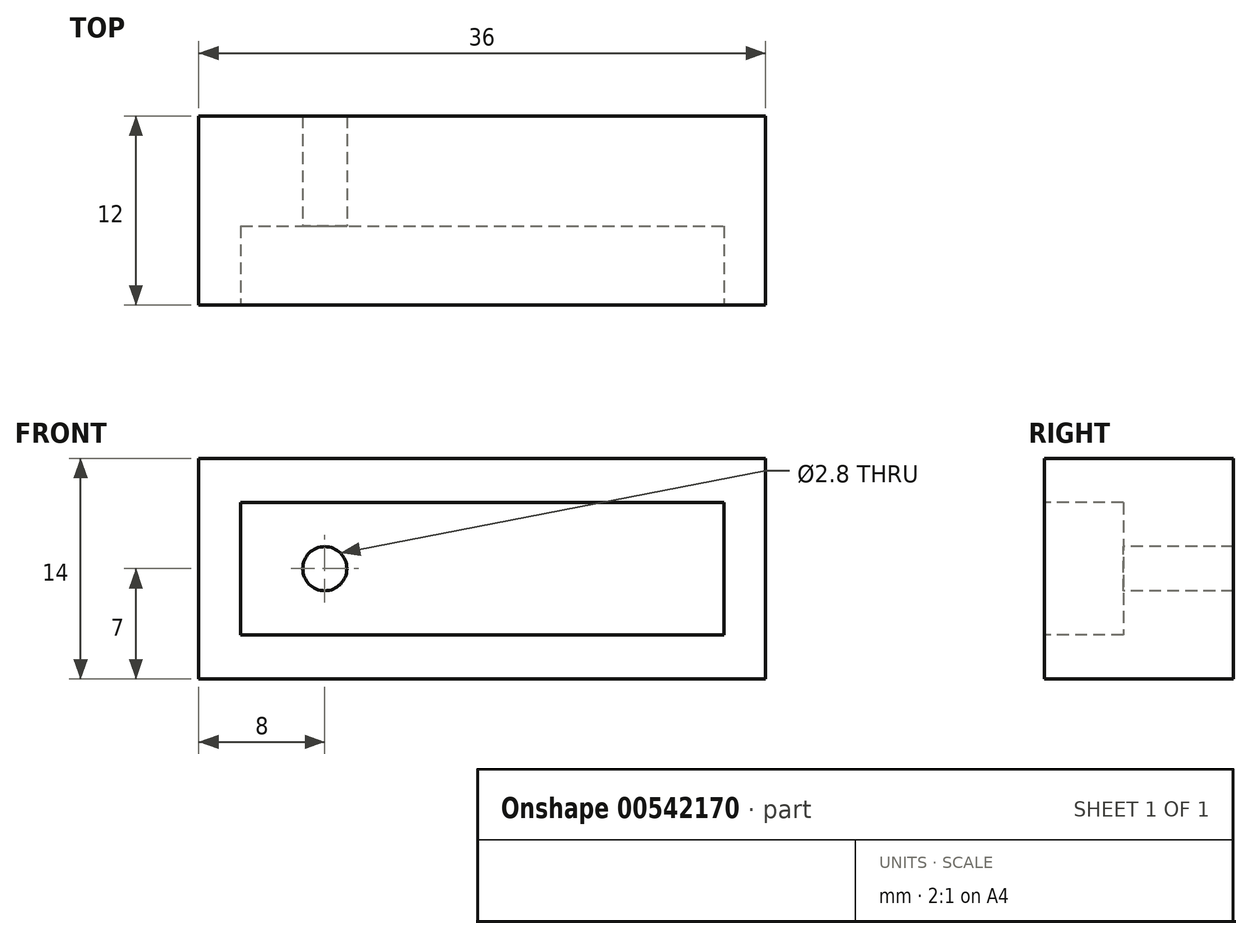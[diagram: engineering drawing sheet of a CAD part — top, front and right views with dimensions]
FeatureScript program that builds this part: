
annotation { "Feature Type Name" : "Feature", "Feature Type Description" : "" }
export const myFeature = defineFeature(function(context is Context, id is Id, definition is map)
    precondition{}
    {
        {
            var Q0;
            Q0=qCreatedBy(makeId("Front.planeOp"),FACE);
            var sketch = newSketch(context, id + "F0", { "sketchPlane" : qUnion([Q0])});
            skLineSegment(sketch, "E0.bottom", {"start": v(-18, 7) * mm, "end": v(18, 7) * mm});
            skLineSegment(sketch, "E0.top", {"start": v(-18, -7) * mm, "end": v(18, -7) * mm});
            skLineSegment(sketch, "E0.left", {"start": v(-18, 7) * mm, "end": v(-18, -7) * mm});
            skLineSegment(sketch, "E0.right", {"start": v(18, 7) * mm, "end": v(18, -7) * mm});
            skSolve(sketch);
        }
        {
            var Q0;
            Q0 = qSketchRegion(id + "F0", true);
            extrude(context, id + "F1", {"entities" : qUnion([Q0]), "depth" : 12 * mm, "offsetDistance" : 25 * mm});
        }
        {
            var Q0;
            Q0=makeQuery(id+"F1.opExtrude","CAP_FACE",FACE,{"disambiguationData":[OSD([sQuery(id+"F0.wireOp",EDGE,"E0.bottom"),sQuery(id+"F0.wireOp",EDGE,"E0.top"),sQuery(id+"F0.wireOp",EDGE,"E0.left"),sQuery(id+"F0.wireOp",EDGE,"E0.right")])],"isStart":false});
            var sketch = newSketch(context, id + "F2", { "sketchPlane" : qUnion([Q0])});
            skLineSegment(sketch, "E1.bottom", {"start": v(-15.35, 4.2) * mm, "end": v(15.35, 4.2) * mm});
            skLineSegment(sketch, "E1.top", {"start": v(-15.35, -4.2) * mm, "end": v(15.35, -4.2) * mm});
            skLineSegment(sketch, "E1.left", {"start": v(-15.35, 4.2) * mm, "end": v(-15.35, -4.2) * mm});
            skLineSegment(sketch, "E1.right", {"start": v(15.35, 4.2) * mm, "end": v(15.35, -4.2) * mm});
            skSolve(sketch);
        }
        {
            var Q0;
            Q0 = qSketchRegion(id + "F2", true);
            extrude(context, id + "F3", {"entities" : qUnion([Q0]), "operationType" : NewBodyOperationType.REMOVE, "oppositeDirection" : true, "depth" : 5 * mm, "offsetDistance" : 25 * mm});
        }
        {
            var Q0;
            Q0=makeQuery(id+"F3.boolean.opBoolean","COPY",FACE,{"derivedFrom":makeQuery(id+"F3.opExtrude","CAP_FACE",FACE,{"disambiguationData":[OSD([sQuery(id+"F2.wireOp",EDGE,"E1.bottom"),sQuery(id+"F2.wireOp",EDGE,"E1.top"),sQuery(id+"F2.wireOp",EDGE,"E1.left"),sQuery(id+"F2.wireOp",EDGE,"E1.right")])],"isStart":false})});
            var sketch = newSketch(context, id + "F4", { "sketchPlane" : qUnion([Q0])});
            skCircle(sketch, "E2", {"center": v(-10, 0) * mm, "radius": 1.4 * mm});
            skSolve(sketch);
        }
        {
            var Q0;
            Q0 = qSketchRegion(id + "F4", true);
            extrude(context, id + "F5", {"entities" : qUnion([Q0]), "operationType" : NewBodyOperationType.REMOVE, "endBound" : BoundingType.UP_TO_NEXT, "oppositeDirection" : true, "depth" : 25 * mm, "offsetDistance" : 25 * mm});
        }
    });
